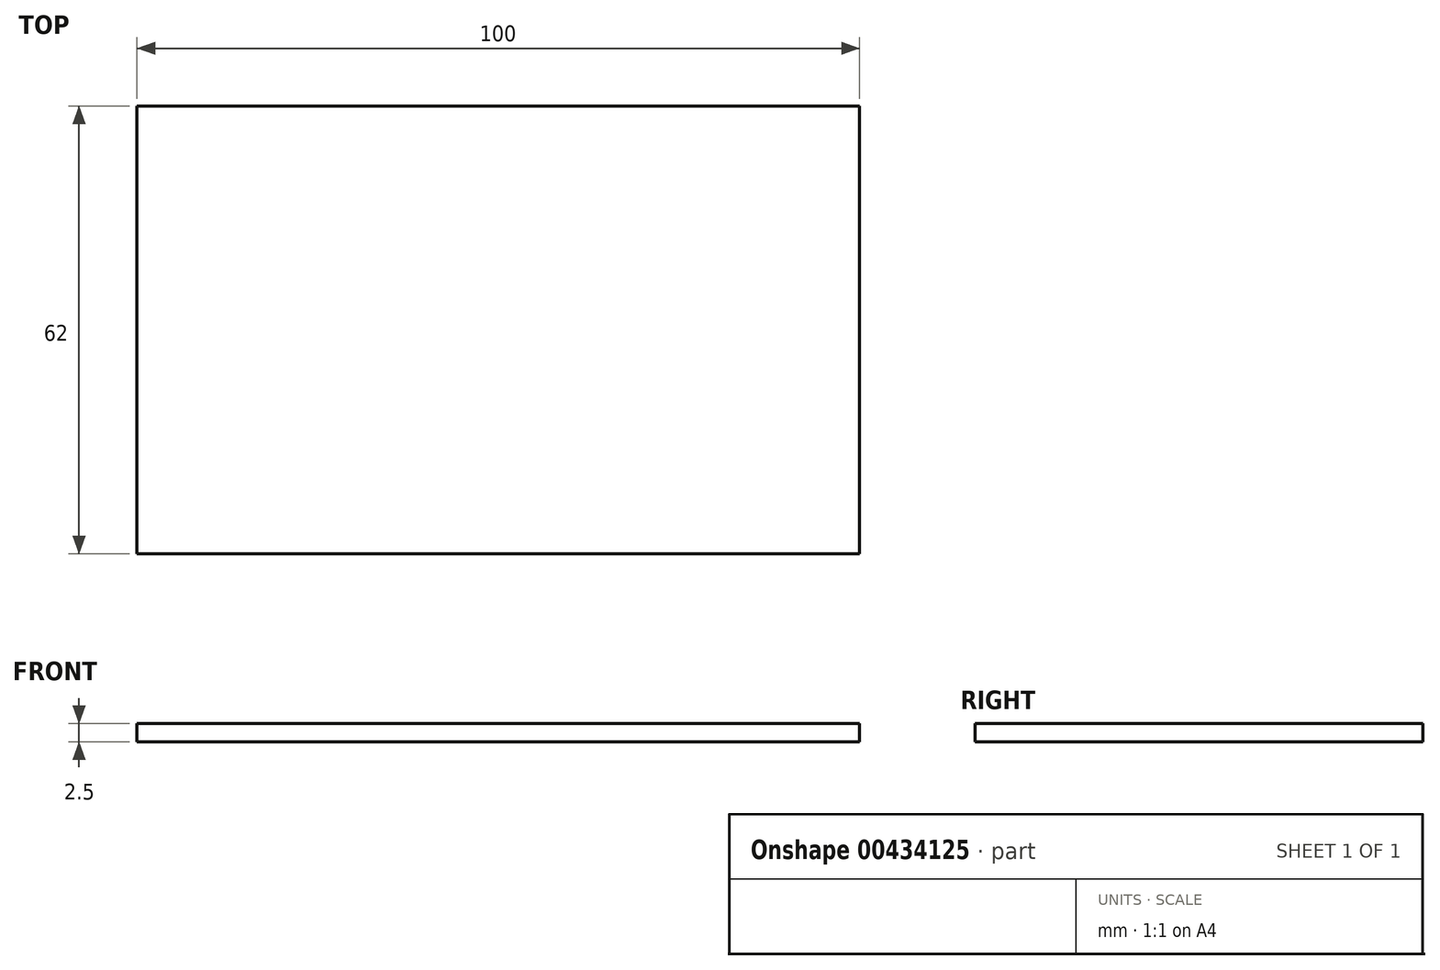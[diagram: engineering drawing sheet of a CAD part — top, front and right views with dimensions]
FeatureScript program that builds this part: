
annotation { "Feature Type Name" : "Feature", "Feature Type Description" : "" }
export const myFeature = defineFeature(function(context is Context, id is Id, definition is map)
    precondition{}
    {
        {
            var Q0;
            Q0=qCreatedBy(makeId("Top.planeOp"),FACE);
            var sketch = newSketch(context, id + "F0", { "sketchPlane" : qUnion([Q0])});
            skLineSegment(sketch, "E0.bottom", {"start": v(-40, 31) * mm, "end": v(60, 31) * mm});
            skLineSegment(sketch, "E0.top", {"start": v(-40, -31) * mm, "end": v(60, -31) * mm});
            skLineSegment(sketch, "E0.left", {"start": v(-40, 31) * mm, "end": v(-40, -31) * mm});
            skLineSegment(sketch, "E0.right", {"start": v(60, 31) * mm, "end": v(60, -31) * mm});
            skSolve(sketch);
        }
        {
            var Q0;
            Q0 = qSketchRegion(id + "F0", true);
            extrude(context, id + "F1", {"entities" : qUnion([Q0]), "depth" : 2.5 * mm});
        }
    });
